# Revit family: Spannbügel
name_source: partatom
category: HLS-Bauteile
revit_build: Autodesk Revit 2017 (Build: 20190507_1515(x64)
units: mm (PartAtom-declared; Revit-internal decimal feet)

## family parameters
Arbeitsebenenbasiert = Ja
Beim Laden mit Abzugskörper schneiden = Nein
Bemaßung runder Anschluss = Durchmesser verwenden
Gemeinsam genutzt = Ja
Immer vertikal = Nein
Raumberechnungspunkt = Nein
Teiletyp = Normal

## types (5) — shared parameters
Fabrikat = MEFA
Firma = MEFA Befestigungs- und Montagesysteme GmbH
Material = Stahl
Oberflaeche = galvanisch verzinkt
Profil = C-Profil
S = 6 mm  [stored 0.019685 ft]
Vorgabe-Ansicht = 1219 mm
max. zul. Last Fx = 0.00 kN
max. zul. Last Fy = 0.00 kN
max. zul. Last Fz = 0.00 kN
min. Randabstand = 70 mm  [stored 0.229659 ft]

## per-type parameters (varying)
| type | Achsabstand U-Bügel | Artikelnummer | B1 | Breite Spannwinkel | EAN | Flachscheibe | Gewicht | Gewicht pro Bauteil | Klemmdicke | Kurztext1 | Kurztext2 | L | Länge U-Bügel | Mutter | Profiltyp | Rundstahl | Spanwinkel |
| Spannbügel M 8 35 | 48 mm | 0816710 | 48 mm  [stored 0.15748 ft] | 70 mm | 4250928420459 | Unterlegscheibe : Unterlegscheibe 8.4x16x1.6 | 0.31 kg | 0.31 kg | 26 mm | Spannbügel M8 C-Profil 35 | Profilhöhe 20 - 42 mm Klemmdicke 26 mm | 56 mm  [stored 0.183727 ft] | 100 mm | Sechskantmutter : Sechskantmutter M10 | 35, Stex 35 | Rundstahl U-Bügel : Rundstahl U Bügel 48-100 M8 | Spannwinkel : Spanwinkel70/20/6 |
| Spannbügel M10 45- 60 | 56 mm | 0816720 | 56 mm  [stored 0.183727 ft] | 80 mm | 4250928420466 | Unterlegscheibe : Unterlegscheibe 10.5x20x2 | 0.40 kg | 0.40 kg | 26 mm | Spannbügel M10 C-Profil 45 | Profilhöhe 26 - 60 mm Klemmdicke 26 mm | 80 mm  [stored 0.262467 ft] | 100 mm | Sechskantmutter : Sechskantmutter M10 | 45 | Rundstahl U-Bügel : Rundstahl U Bügel 56-100 M10 | Spannwinkel : Spanwinkel 80/20/6 |
| Spannbügel M10 45- 90 | 56 mm | 0816730 | 56 mm  [stored 0.183727 ft] | 80 mm | 4250928420473 | Unterlegscheibe : Unterlegscheibe 10.5x20x2 | 0.44 kg | 0.44 kg | 26 mm | Spannbügel M10 C-Profil 45 | Profilhöhe 75 + 90 mm Klemmdicke 26 mm | 110 mm  [stored 0.360892 ft] | 140 mm | Sechskantmutter : Sechskantmutter M10 | 45 | Rundstahl U-Bügel : Rundstahl U Bügel 56-140 M10 | Spannwinkel : Spanwinkel 80/20/6 |
| Spannbügel M12 45- 90 | 59 mm | 08167401 | 59 mm | 110 mm | 4250928420480 | Unterlegscheibe : Unterlegscheibe 13x24x2.5 | 0.75 kg | 0.75 kg | 29 mm | Spannbügel M12 C-Profil 45 | Profilhöhe 75 + 90 mm Klemmdicke 29 mm | 110 mm  [stored 0.360892 ft] | 150 mm | Sechskantmutter : Sechskantmutter M12 | 45 | Rundstahl U-Bügel : Rundstahl U Bügel 59-150 M12 | Spannwinkel : Spanwinkel 100/22/8 |
| Spannbügel M12 45-150 | 59 mm | 08167501 | 59 mm | 100 mm | 4250928420497 | Unterlegscheibe : Unterlegscheibe 13x24x2.5 | 0.83 kg | 0.83 kg | 29 mm | Spannbügel M12 C-Profil 45 | Profilhöhe 120 + 150 mm Klemmdicke 29 mm | 170 mm  [stored 0.557743 ft] | 210 mm | Sechskantmutter : Sechskantmutter M12 | 45 | Rundstahl U-Bügel : Rundstahl U Bügel 59-210 M12 | Spannwinkel : Spanwinkel 100/22/8 |

note: [stored X ft] marks values corroborated as IEEE doubles in the binary element streams (Revit-internal decimal feet)

## geometry (parser evidence)
native form markers: Sweep x3
no freeform markers — native parametric forms only
